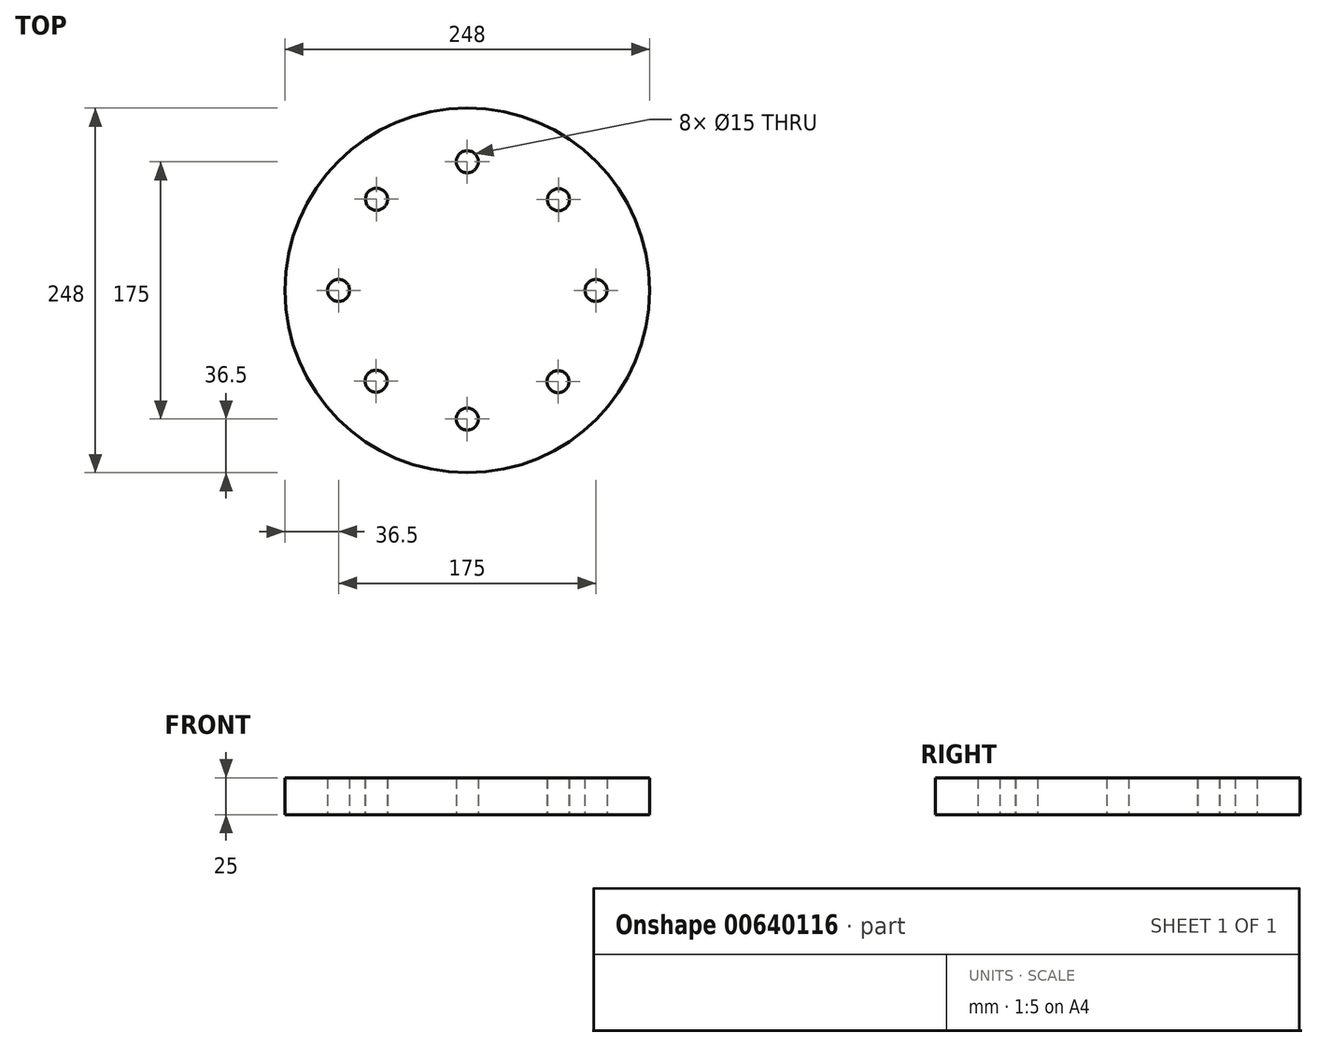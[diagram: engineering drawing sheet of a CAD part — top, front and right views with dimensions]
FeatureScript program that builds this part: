
annotation { "Feature Type Name" : "Feature", "Feature Type Description" : "" }
export const myFeature = defineFeature(function(context is Context, id is Id, definition is map)
    precondition{}
    {
        {
            var Q0;
            Q0=qCreatedBy(makeId("Top.planeOp"),FACE);
            var sketch = newSketch(context, id + "F0", { "sketchPlane" : qUnion([Q0])});
            skCircle(sketch, "E0", {"center": v(0, 0) * mm, "radius": 124 * mm});
            skLineSegment(sketch, "E1.right", {"start": v(-40, -39.8) * mm, "end": v(-40, -40) * mm});
            skLineSegment(sketch, "E2.top", {"start": v(39.8, -40) * mm, "end": v(40, -40) * mm});
            skCircle(sketch, "E3", {"center": v(0, 87.5) * mm, "radius": 7.5 * mm});
            skCircle(sketch, "E4", {"center": v(0, -87.5) * mm, "radius": 7.5 * mm});
            skCircle(sketch, "E5", {"center": v(-62.03, -61.72) * mm, "radius": 7.5 * mm});
            skCircle(sketch, "E6", {"center": v(61.72, -62.03) * mm, "radius": 7.5 * mm});
            skCircle(sketch, "E7", {"center": v(87.5, 0) * mm, "radius": 7.5 * mm});
            skCircle(sketch, "E8", {"center": v(-87.5, 0) * mm, "radius": 7.5 * mm});
            skCircle(sketch, "E9", {"center": v(-61.72, 62.03) * mm, "radius": 7.5 * mm});
            skCircle(sketch, "E10", {"center": v(62.03, 61.72) * mm, "radius": 7.5 * mm});
            skLineSegment(sketch, "E11.trimOffspring", {"start": v(87.9, 87.46) * mm, "end": v(88.34, 87.9) * mm});
            skPoint(sketch, "E12.orphan", {"position": v(-87.46, -87.03) * mm});
            skPoint(sketch, "E13.orphan", {"position": v(-87.46, 87.9) * mm});
            skPoint(sketch, "E14.top.end.orphan", {"position": v(-40, 40) * mm});
            skPoint(sketch, "E15.right.end.orphan", {"position": v(40, 40) * mm});
            skSolve(sketch);
        }
        {
            var Q0;
            Q0=makeQuery(id+"F0.imprint","IMPRINT",FACE,{"disambiguationData":[TD([[makeQuery(id+"F0.imprint","IMPRINT",EDGE,{"derivedFrom":sQuery(id+"F0.wireOp",EDGE,"E0")}),1.0]])]});
            extrude(context, id + "F1", {"entities" : qUnion([Q0]), "depth" : 25 * mm, "offsetDistance" : 25 * mm});
        }
    });
